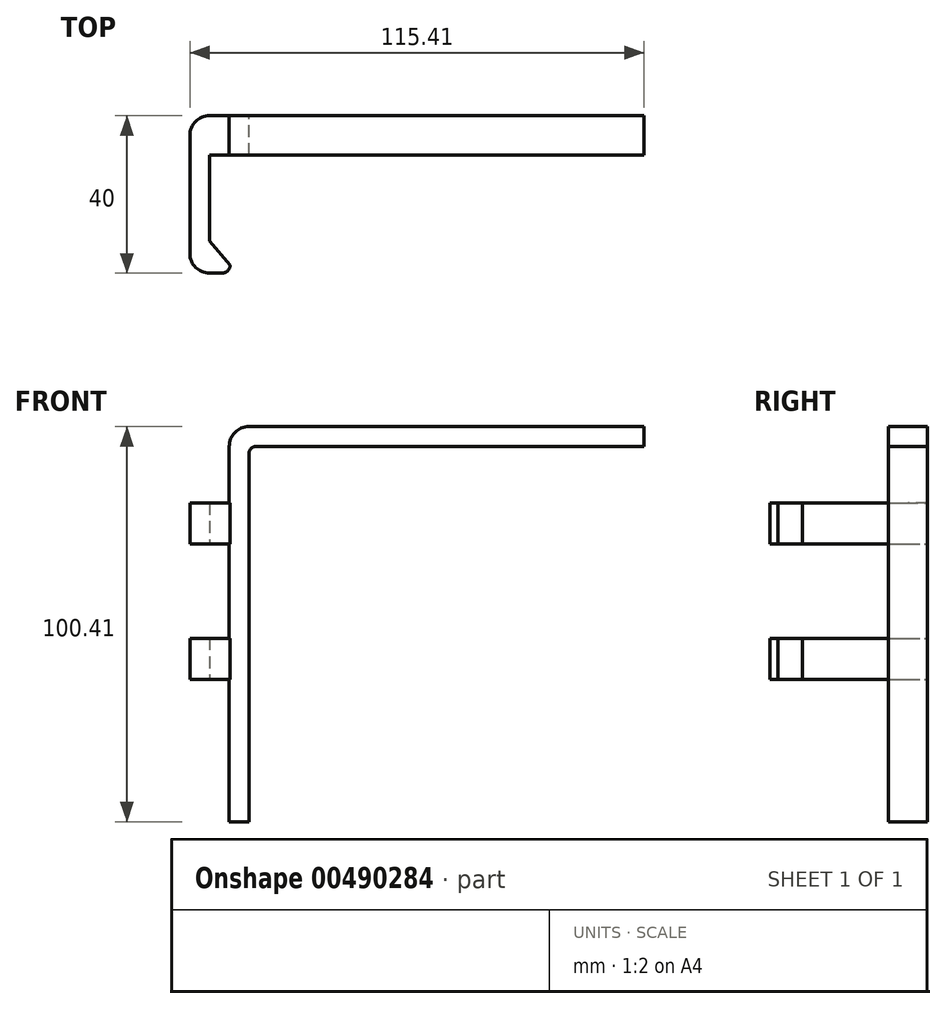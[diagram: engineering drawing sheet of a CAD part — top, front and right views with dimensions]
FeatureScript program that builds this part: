
annotation { "Feature Type Name" : "Feature", "Feature Type Description" : "" }
export const myFeature = defineFeature(function(context is Context, id is Id, definition is map)
    precondition{}
    {
        {
            var Q0;
            Q0=qCreatedBy(makeId("Front.planeOp"),FACE);
            var sketch = newSketch(context, id + "F0", { "sketchPlane" : qUnion([Q0])});
            skLineSegment(sketch, "E0.bottom", {"start": v(0, -51.3) * mm, "end": v(-5, -51.3) * mm});
            skLineSegment(sketch, "E0.top", {"start": v(0, 49.1) * mm, "end": v(0, 49.1) * mm});
            skLineSegment(sketch, "E0.left", {"start": v(0, -51.3) * mm, "end": v(0, 42.1) * mm});
            skLineSegment(sketch, "E0.right", {"start": v(-5, -51.3) * mm, "end": v(-5, -15.1) * mm});
            skLineSegment(sketch, "E1.bottom", {"start": v(100.4, 49.1) * mm, "end": v(100.4, 44.1) * mm});
            skLineSegment(sketch, "E1.left", {"start": v(100.4, 49.1) * mm, "end": v(0, 49.1) * mm});
            skLineSegment(sketch, "E1.right", {"start": v(100.4, 44.1) * mm, "end": v(2, 44.1) * mm});
            skPoint(sketch, "E2.visualSharp", {"position": v(-5, 49.1) * mm});
            skArc(sketch, "E2.filletArc", {"start": v(0, 49.1) * mm, "mid": v(-3.54, 47.63) * mm, "end": v(-5, 44.1) * mm});
            skLineSegment(sketch, "E3", {"start": v(-5, 29.68) * mm, "end": v(-5, 44.1) * mm});
            skLineSegment(sketch, "E4", {"start": v(-5, 19.25) * mm, "end": v(-15, 19.25) * mm});
            skLineSegment(sketch, "E5", {"start": v(-15, 29.68) * mm, "end": v(-5, 29.68) * mm});
            skLineSegment(sketch, "E6", {"start": v(-15, 19.25) * mm, "end": v(-15, 29.68) * mm});
            skLineSegment(sketch, "E7.bottom", {"start": v(-5, -4.68) * mm, "end": v(-15, -4.68) * mm});
            skLineSegment(sketch, "E7.top", {"start": v(-5, -15.1) * mm, "end": v(-15, -15.1) * mm});
            skLineSegment(sketch, "E7.right", {"start": v(-15, -4.68) * mm, "end": v(-15, -15.1) * mm});
            skLineSegment(sketch, "E8.trimOffspring", {"start": v(-5, -4.68) * mm, "end": v(-5, 19.25) * mm});
            skArc(sketch, "E9.filletArc", {"start": v(2, 44.1) * mm, "mid": v(0.59, 43.51) * mm, "end": v(0, 42.1) * mm});
            skSolve(sketch);
        }
        {
            var Q0;
            Q0=makeQuery(id+"F0.imprint","IMPRINT",FACE,{"disambiguationData":[TD([[makeQuery(id+"F0.imprint","IMPRINT",EDGE,{"derivedFrom":sQuery(id+"F0.wireOp",EDGE,"E0.bottom")}),-1.0]])]});
            extrude(context, id + "F1", {"entities" : qUnion([Q0]), "depth" : 10 * mm});
        }
        {
            var Q0;
            Q0=makeQuery(id+"F1.opExtrude","CAP_FACE",FACE,{"disambiguationData":[OSD([sQuery(id+"F0.wireOp",EDGE,"E0.bottom"),sQuery(id+"F0.wireOp",EDGE,"E0.left"),sQuery(id+"F0.wireOp",EDGE,"E0.right"),sQuery(id+"F0.wireOp",EDGE,"E1.bottom"),sQuery(id+"F0.wireOp",EDGE,"E1.left"),sQuery(id+"F0.wireOp",EDGE,"E1.right"),sQuery(id+"F0.wireOp",EDGE,"E2.filletArc"),sQuery(id+"F0.wireOp",EDGE,"E3"),sQuery(id+"F0.wireOp",EDGE,"E4"),sQuery(id+"F0.wireOp",EDGE,"E5"),sQuery(id+"F0.wireOp",EDGE,"E6"),sQuery(id+"F0.wireOp",EDGE,"E7.bottom"),sQuery(id+"F0.wireOp",EDGE,"E7.top"),sQuery(id+"F0.wireOp",EDGE,"E7.right"),sQuery(id+"F0.wireOp",EDGE,"E8.trimOffspring"),sQuery(id+"F0.wireOp",EDGE,"E9.filletArc")])],"isStart":false});
            var sketch = newSketch(context, id + "F2", { "sketchPlane" : qUnion([Q0])});
            skLineSegment(sketch, "E10.bottom", {"start": v(-15, 29.68) * mm, "end": v(-10, 29.68) * mm});
            skLineSegment(sketch, "E10.top", {"start": v(-15, 19.25) * mm, "end": v(-10, 19.25) * mm});
            skLineSegment(sketch, "E10.left", {"start": v(-15, 29.68) * mm, "end": v(-15, 19.25) * mm});
            skLineSegment(sketch, "E10.right", {"start": v(-10, 29.68) * mm, "end": v(-10, 19.25) * mm});
            skLineSegment(sketch, "E11.bottom", {"start": v(-15, -4.68) * mm, "end": v(-10, -4.68) * mm});
            skLineSegment(sketch, "E11.top", {"start": v(-15, -15.1) * mm, "end": v(-10, -15.1) * mm});
            skLineSegment(sketch, "E11.left", {"start": v(-15, -4.68) * mm, "end": v(-15, -15.1) * mm});
            skLineSegment(sketch, "E11.right", {"start": v(-10, -4.68) * mm, "end": v(-10, -15.1) * mm});
            skSolve(sketch);
        }
        {
            var Q0;
            Q0 = qSketchRegion(id + "F2", true);
            extrude(context, id + "F3", {"entities" : qUnion([Q0]), "operationType" : NewBodyOperationType.ADD, "depth" : 30 * mm});
        }
        {
            var Q0;
            Q0=makeQuery(id+"F3.opExtrude","CAP_EDGE",EDGE,{"disambiguationData":[OSD([sQuery(id+"F2.wireOp",EDGE,"E10.left")])],"isStart":false});
            var Q1;
            Q1=makeQuery(id+"F3.opExtrude","CAP_EDGE",EDGE,{"disambiguationData":[OSD([sQuery(id+"F2.wireOp",EDGE,"E11.left")])],"isStart":false});
            var Q2;
            Q2=makeQuery(id+"F1.opExtrude","CAP_EDGE",EDGE,{"disambiguationData":[OSD([sQuery(id+"F0.wireOp",EDGE,"E6")])],"isStart":true});
            var Q3;
            Q3=makeQuery(id+"F1.opExtrude","CAP_EDGE",EDGE,{"disambiguationData":[OSD([sQuery(id+"F0.wireOp",EDGE,"E7.right")])],"isStart":true});
            fillet(context, id + "F4", {"entities" : qUnion([Q0, Q1, Q2, Q3]), "radius" : 5 * mm, "tangentPropagation" : true, "allowEdgeOverflow" : false});
        }
        {
            var Q0;
            Q0=makeQuery(id+"F3.boolean.opBoolean","MERGE",FACE,{"derivedFrom":[makeQuery(id+"F1.opExtrude","SWEPT_FACE",FACE,{"disambiguationData":[OSD([sQuery(id+"F0.wireOp",EDGE,"E7.top")])]}),makeQuery(id+"F3.opExtrude","SWEPT_FACE",FACE,{"disambiguationData":[OSD([sQuery(id+"F2.wireOp",EDGE,"E11.top")])]})]});
            var sketch = newSketch(context, id + "F5", { "sketchPlane" : qUnion([Q0])});
            skLineSegment(sketch, "E12", {"start": v(-10, 40) * mm, "end": v(-6.8, 40) * mm});
            skLineSegment(sketch, "E13", {"start": v(-4.8, 38) * mm, "end": v(-10, 31.81) * mm});
            skLineSegment(sketch, "E14", {"start": v(-10, 31.81) * mm, "end": v(-10, 40) * mm});
            skPoint(sketch, "E15.visualSharp", {"position": v(-4.8, 40) * mm});
            skArc(sketch, "E15.filletArc", {"start": v(-4.8, 38) * mm, "mid": v(-5.4, 39.41) * mm, "end": v(-6.8, 40) * mm});
            skSolve(sketch);
        }
        {
            var Q0;
            Q0 = qSketchRegion(id + "F5", true);
            var Q1;
            Q1=makeQuery(id+"F3.boolean.opBoolean","MERGE",FACE,{"derivedFrom":[makeQuery(id+"F1.opExtrude","SWEPT_FACE",FACE,{"disambiguationData":[OSD([sQuery(id+"F0.wireOp",EDGE,"E7.bottom")])]}),makeQuery(id+"F3.opExtrude","SWEPT_FACE",FACE,{"disambiguationData":[OSD([sQuery(id+"F2.wireOp",EDGE,"E11.bottom")])]})]});
            extrude(context, id + "F6", {"entities" : qUnion([Q0]), "operationType" : NewBodyOperationType.ADD, "endBound" : BoundingType.UP_TO_SURFACE, "oppositeDirection" : true, "endBoundEntityFace" : qUnion([Q1]), "depth" : 25 * mm});
        }
        {
            var Q0;
            Q0=makeQuery(id+"F3.boolean.opBoolean","MERGE",FACE,{"derivedFrom":[makeQuery(id+"F1.opExtrude","SWEPT_FACE",FACE,{"disambiguationData":[OSD([sQuery(id+"F0.wireOp",EDGE,"E4")])]}),makeQuery(id+"F3.opExtrude","SWEPT_FACE",FACE,{"disambiguationData":[OSD([sQuery(id+"F2.wireOp",EDGE,"E10.top")])]})]});
            var sketch = newSketch(context, id + "F7", { "sketchPlane" : qUnion([Q0])});
            skLineSegment(sketch, "E16", {"start": v(-10, 40) * mm, "end": v(-6.8, 40) * mm});
            skLineSegment(sketch, "E17", {"start": v(-4.8, 38) * mm, "end": v(-10, 31.81) * mm});
            skLineSegment(sketch, "E18", {"start": v(-10, 31.81) * mm, "end": v(-10, 40) * mm});
            skPoint(sketch, "E19.visualSharp", {"position": v(-4.8, 40) * mm});
            skArc(sketch, "E19.filletArc", {"start": v(-4.8, 38) * mm, "mid": v(-5.4, 39.41) * mm, "end": v(-6.8, 40) * mm});
            skSolve(sketch);
        }
        {
            var Q0;
            Q0 = qSketchRegion(id + "F7", true);
            var Q1;
            Q1=makeQuery(id+"F3.boolean.opBoolean","MERGE",FACE,{"derivedFrom":[makeQuery(id+"F1.opExtrude","SWEPT_FACE",FACE,{"disambiguationData":[OSD([sQuery(id+"F0.wireOp",EDGE,"E5")])]}),makeQuery(id+"F3.opExtrude","SWEPT_FACE",FACE,{"disambiguationData":[OSD([sQuery(id+"F2.wireOp",EDGE,"E10.bottom")])]})]});
            extrude(context, id + "F8", {"entities" : qUnion([Q0]), "operationType" : NewBodyOperationType.ADD, "endBound" : BoundingType.UP_TO_SURFACE, "oppositeDirection" : true, "endBoundEntityFace" : qUnion([Q1]), "depth" : 25 * mm});
        }
    });
